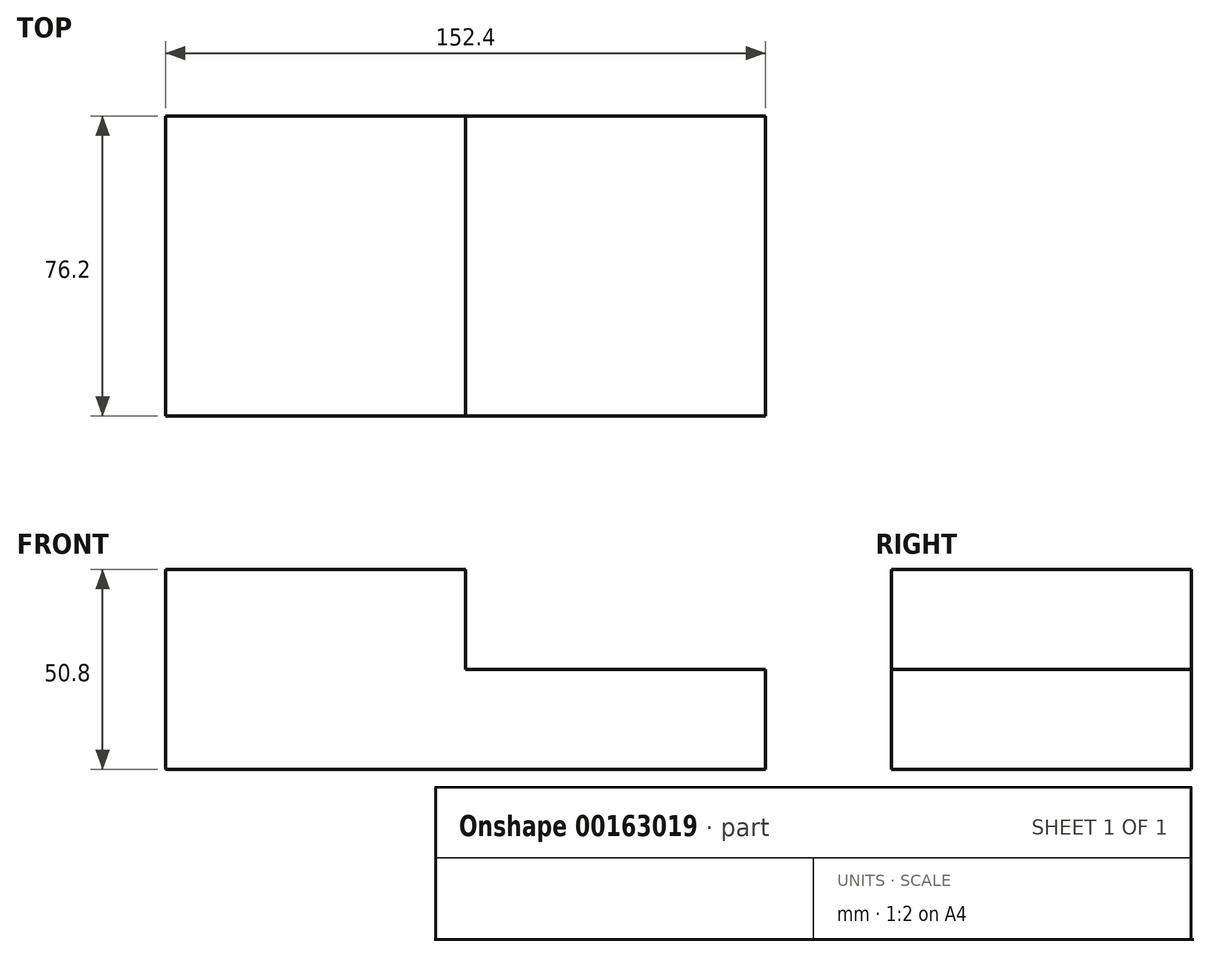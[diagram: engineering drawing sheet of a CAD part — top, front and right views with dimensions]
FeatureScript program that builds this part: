
annotation { "Feature Type Name" : "Feature", "Feature Type Description" : "" }
export const myFeature = defineFeature(function(context is Context, id is Id, definition is map)
    precondition{}
    {
        {
            var Q0;
            Q0=qCreatedBy(makeId("Front.planeOp"),FACE);
            var sketch = newSketch(context, id + "F0", { "sketchPlane" : qUnion([Q0])});
            skLineSegment(sketch, "E0", {"start": v(0, 0) * mm, "end": v(76.2, 0) * mm});
            skLineSegment(sketch, "E1", {"start": v(76.2, 0) * mm, "end": v(76.2, 25.4) * mm});
            skLineSegment(sketch, "E2", {"start": v(76.2, 25.4) * mm, "end": v(0, 25.4) * mm});
            skLineSegment(sketch, "E3", {"start": v(0, 25.4) * mm, "end": v(0, 50.8) * mm});
            skLineSegment(sketch, "E4", {"start": v(0, 50.8) * mm, "end": v(-76.2, 50.8) * mm});
            skLineSegment(sketch, "E5", {"start": v(-76.2, 0) * mm, "end": v(0, 0) * mm});
            skLineSegment(sketch, "E6", {"start": v(-76.2, 0) * mm, "end": v(-76.2, 50.8) * mm});
            skSolve(sketch);
        }
        {
            var Q0;
            Q0=makeQuery(id+"F0.imprint","IMPRINT",FACE,{"disambiguationData":[TD([[makeQuery(id+"F0.imprint","IMPRINT",EDGE,{"derivedFrom":sQuery(id+"F0.wireOp",EDGE,"E0")}),1.0]])]});
            extrude(context, id + "F1", {"entities" : qUnion([Q0]), "depth" : 76.2 * mm});
        }
    });
